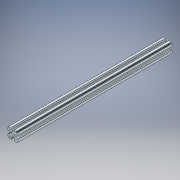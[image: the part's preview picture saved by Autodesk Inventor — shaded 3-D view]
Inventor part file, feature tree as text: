
AUTODESK INVENTOR PART (.ipt)
format: ipt  version: 2017 (Build 210142000, 142)  size: 300,544 bytes
history: native  units: in
note: dims shown in document units (in); Inventor stores cm internally (conversion verified against a paired STEP export)
features: extrude x1, sketch x1, fillet x1
ambient origin geometry x8: Origin, YZ Plane, XZ Plane, XY Plane, X Axis, Y Axis, Z Axis, Center Point
bodies: Solid1 (feature_tree)
feature tree (3):
  extrude  "Extrusion1"  [1 undecoded]
  sketch  "Sketch2"  dims[d0=57.0in d1=0.0in]
  fillet  "Fillet10"  [1 undecoded]
note: 2 required parameter values undecoded (feature->parameter linkage not recoverable at this tier; creation-order binding heuristic only, values carry confidence <= 0.55)
